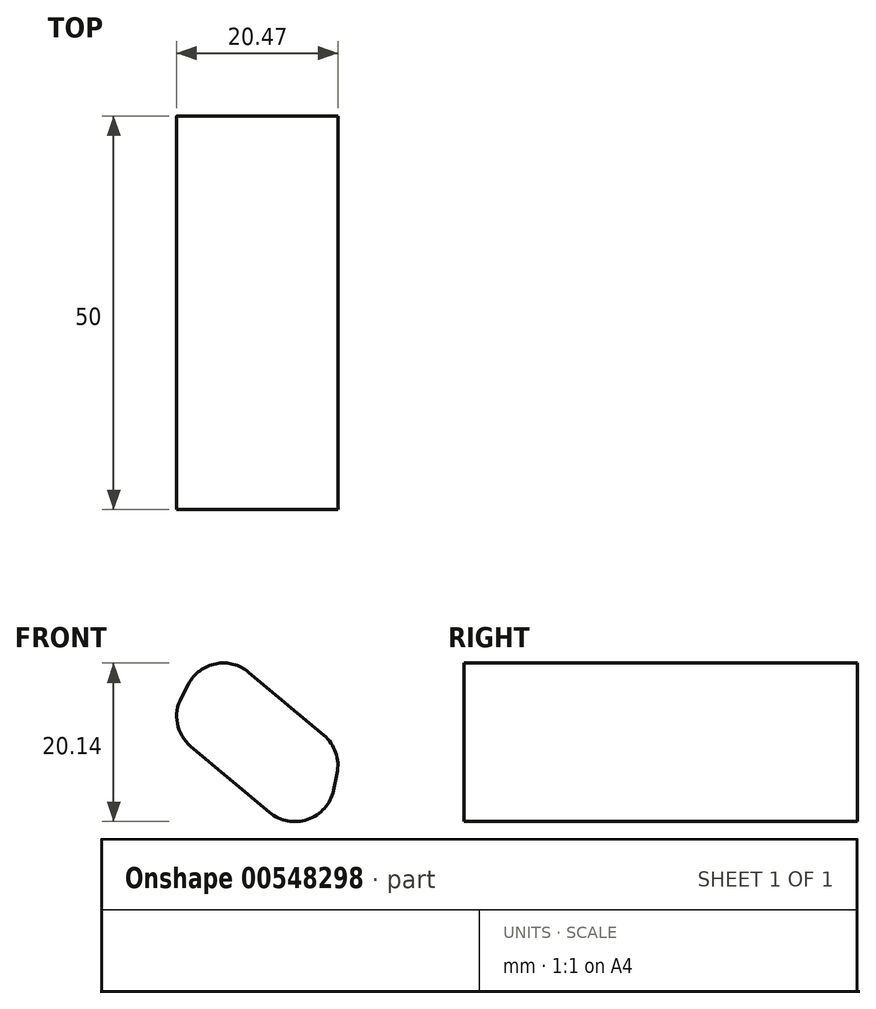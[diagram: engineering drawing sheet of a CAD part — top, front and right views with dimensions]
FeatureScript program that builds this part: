
annotation { "Feature Type Name" : "Feature", "Feature Type Description" : "" }
export const myFeature = defineFeature(function(context is Context, id is Id, definition is map)
    precondition{}
    {
        {
            var Q0;
            Q0=qCreatedBy(makeId("Top.planeOp"),FACE);
            var sketch = newSketch(context, id + "F0", { "sketchPlane" : qUnion([Q0])});
            skLineSegment(sketch, "E0.bottom", {"start": v(-14.85, -25) * mm, "end": v(14.85, -25) * mm});
            skLineSegment(sketch, "E0.top", {"start": v(-14.85, 25) * mm, "end": v(14.85, 25) * mm});
            skLineSegment(sketch, "E0.left", {"start": v(-14.85, -25) * mm, "end": v(-14.85, 25) * mm});
            skLineSegment(sketch, "E0.right", {"start": v(14.85, -25) * mm, "end": v(14.85, 25) * mm});
            skPoint(sketch, "E0.middle", {"position": v(0, 0) * mm});
            skSolve(sketch);
        }
        {
            var Q0;
            Q0=makeQuery(id+"F0.imprint","IMPRINT",FACE,{"disambiguationData":[TD([[makeQuery(id+"F0.imprint","IMPRINT",EDGE,{"derivedFrom":sQuery(id+"F0.wireOp",EDGE,"E0.bottom")}),1.0]])]});
            extrude(context, id + "F1", {"entities" : qUnion([Q0]), "depth" : 11.93 * mm, "offsetDistance" : 25 * mm});
        }
        {
            var Q0;
            Q0=makeQuery(id+"F1.opExtrude","CAP_EDGE",EDGE,{"disambiguationData":[OSD([sQuery(id+"F0.wireOp",EDGE,"E0.right")])],"isStart":false});
            chamfer(context, id + "F2", {"entities" : qUnion([Q0]), "chamferType" : ChamferType.OFFSET_ANGLE, "width" : 8 * mm, "oppositeDirection" : false, "angle" : 62 * degree, "tangentPropagation" : true});
        }
        {
            var Q0;
            Q0=makeQuery(id+"F1.opExtrude","CAP_EDGE",EDGE,{"disambiguationData":[OSD([sQuery(id+"F0.wireOp",EDGE,"E0.left")])],"isStart":true});
            chamfer(context, id + "F3", {"entities" : qUnion([Q0]), "chamferType" : ChamferType.OFFSET_ANGLE, "width" : 2.6 * mm, "oppositeDirection" : false, "angle" : 78 * degree, "tangentPropagation" : true});
        }
        {
            var Q0;
            {var subQ0=sQuery(id+"F0.wireOp",EDGE,"E0.left");Q0=makeQuery(id+"F3.opChamfer","BLEND_EDGE",EDGE,{"blendedFrom":[makeQuery(id+"F1.opExtrude","CAP_EDGE",EDGE,{"disambiguationData":[OSD([subQ0])],"isStart":true}),makeQuery(id+"F1.opExtrude","CAP_FACE",FACE,{"disambiguationData":[OSD([sQuery(id+"F0.wireOp",EDGE,"E0.bottom"),sQuery(id+"F0.wireOp",EDGE,"E0.top"),subQ0,sQuery(id+"F0.wireOp",EDGE,"E0.right")])],"isStart":false})],"blendedInto":[makeQuery(id+"F1.opExtrude","CAP_FACE",FACE,{"disambiguationData":[OSD([sQuery(id+"F0.wireOp",EDGE,"E0.bottom"),sQuery(id+"F0.wireOp",EDGE,"E0.top"),subQ0,sQuery(id+"F0.wireOp",EDGE,"E0.right")])],"isStart":false})]});}
            var Q1;
            {var subQ0=sQuery(id+"F0.wireOp",EDGE,"E0.left");Q1=makeQuery(id+"F3.opChamfer","BLEND_EDGE",EDGE,{"blendedFrom":[makeQuery(id+"F1.opExtrude","CAP_EDGE",EDGE,{"disambiguationData":[OSD([subQ0])],"isStart":true}),makeQuery(id+"F1.opExtrude","CAP_FACE",FACE,{"disambiguationData":[OSD([sQuery(id+"F0.wireOp",EDGE,"E0.bottom"),sQuery(id+"F0.wireOp",EDGE,"E0.top"),subQ0,sQuery(id+"F0.wireOp",EDGE,"E0.right")])],"isStart":true})],"blendedInto":[makeQuery(id+"F1.opExtrude","CAP_FACE",FACE,{"disambiguationData":[OSD([sQuery(id+"F0.wireOp",EDGE,"E0.bottom"),sQuery(id+"F0.wireOp",EDGE,"E0.top"),subQ0,sQuery(id+"F0.wireOp",EDGE,"E0.right")])],"isStart":true})]});}
            var Q2;
            {var subQ0=sQuery(id+"F0.wireOp",EDGE,"E0.right");Q2=makeQuery(id+"F2.opChamfer","BLEND_EDGE",EDGE,{"blendedFrom":[makeQuery(id+"F1.opExtrude","CAP_EDGE",EDGE,{"disambiguationData":[OSD([subQ0])],"isStart":false}),makeQuery(id+"F1.opExtrude","CAP_FACE",FACE,{"disambiguationData":[OSD([sQuery(id+"F0.wireOp",EDGE,"E0.bottom"),sQuery(id+"F0.wireOp",EDGE,"E0.top"),sQuery(id+"F0.wireOp",EDGE,"E0.left"),subQ0])],"isStart":false})],"blendedInto":[makeQuery(id+"F1.opExtrude","CAP_FACE",FACE,{"disambiguationData":[OSD([sQuery(id+"F0.wireOp",EDGE,"E0.bottom"),sQuery(id+"F0.wireOp",EDGE,"E0.top"),sQuery(id+"F0.wireOp",EDGE,"E0.left"),subQ0])],"isStart":false})]});}
            var Q3;
            {var subQ0=sQuery(id+"F0.wireOp",EDGE,"E0.right");Q3=makeQuery(id+"F2.opChamfer","BLEND_EDGE",EDGE,{"blendedFrom":[makeQuery(id+"F1.opExtrude","CAP_EDGE",EDGE,{"disambiguationData":[OSD([subQ0])],"isStart":false}),makeQuery(id+"F1.opExtrude","CAP_FACE",FACE,{"disambiguationData":[OSD([sQuery(id+"F0.wireOp",EDGE,"E0.bottom"),sQuery(id+"F0.wireOp",EDGE,"E0.top"),sQuery(id+"F0.wireOp",EDGE,"E0.left"),subQ0])],"isStart":true})],"blendedInto":[makeQuery(id+"F1.opExtrude","CAP_FACE",FACE,{"disambiguationData":[OSD([sQuery(id+"F0.wireOp",EDGE,"E0.bottom"),sQuery(id+"F0.wireOp",EDGE,"E0.top"),sQuery(id+"F0.wireOp",EDGE,"E0.left"),subQ0])],"isStart":true})]});}
            fillet(context, id + "F4", {"entities" : qUnion([Q0, Q1, Q2, Q3]), "radius" : 5 * mm, "tangentPropagation" : true, "allowEdgeOverflow" : false});
        }
        {
            var Q0;
            Q0=makeQuery(id+"F1.opExtrude","SWEPT_BODY",BODY,{"disambiguationData":[OSD([sQuery(id+"F0.wireOp",EDGE,"E0.bottom"),sQuery(id+"F0.wireOp",EDGE,"E0.top"),sQuery(id+"F0.wireOp",EDGE,"E0.left"),sQuery(id+"F0.wireOp",EDGE,"E0.right")])]});
            var Q1;
            {var subQ0=sQuery(id+"F0.wireOp",EDGE,"E0.left");Q1=makeQuery(id+"F4.opFillet","BLEND_EDGE",EDGE,{"blendedFrom":[makeQuery(id+"F3.opChamfer","BLEND_EDGE",EDGE,{"blendedFrom":[makeQuery(id+"F1.opExtrude","CAP_EDGE",EDGE,{"disambiguationData":[OSD([subQ0])],"isStart":true}),makeQuery(id+"F1.opExtrude","CAP_FACE",FACE,{"disambiguationData":[OSD([sQuery(id+"F0.wireOp",EDGE,"E0.bottom"),sQuery(id+"F0.wireOp",EDGE,"E0.top"),subQ0,sQuery(id+"F0.wireOp",EDGE,"E0.right")])],"isStart":false})],"blendedInto":[makeQuery(id+"F1.opExtrude","CAP_FACE",FACE,{"disambiguationData":[OSD([sQuery(id+"F0.wireOp",EDGE,"E0.bottom"),sQuery(id+"F0.wireOp",EDGE,"E0.top"),subQ0,sQuery(id+"F0.wireOp",EDGE,"E0.right")])],"isStart":false})]}),makeQuery(id+"F3.opChamfer","BLEND_FACE",FACE,{"disambiguationData":[OSD([subQ0])]})],"blendedInto":[makeQuery(id+"F3.opChamfer","BLEND_FACE",FACE,{"disambiguationData":[OSD([subQ0])]})]});}
            transform(context, id + "F5", {"entities" : qUnion([Q0]), "transformType" : TransformType.ROTATION, "transformAxis" : qUnion([Q1]), "angle" : 40 * degree, "oppositeDirection" : true, "makeCopy" : false});
        }
    });
